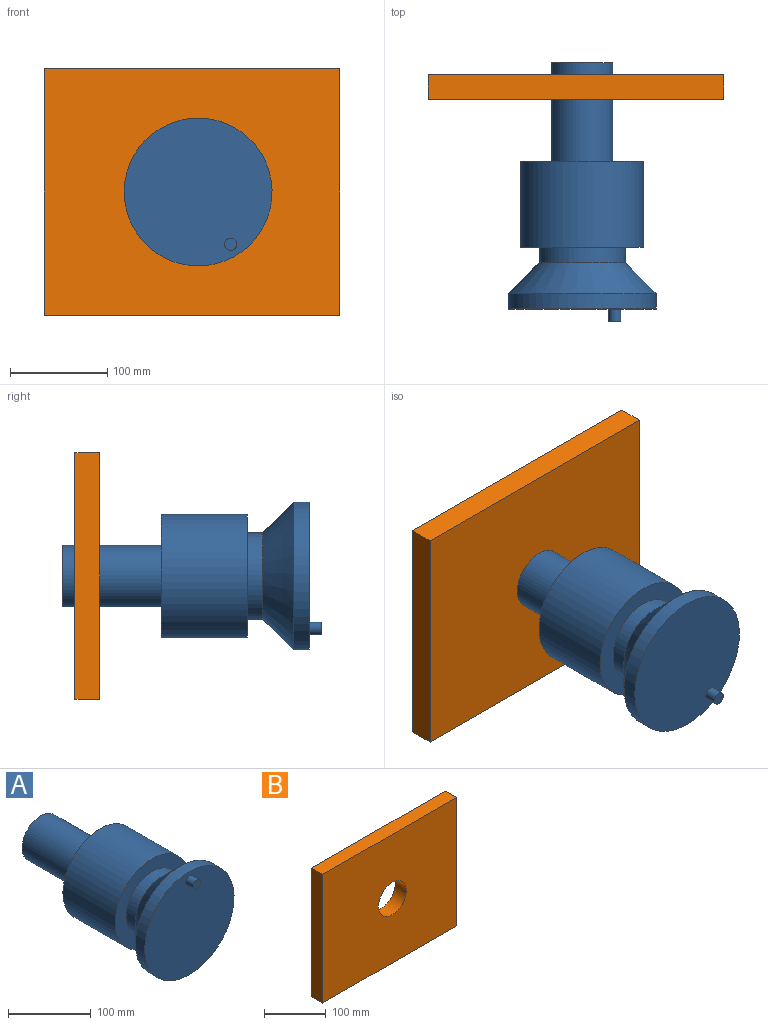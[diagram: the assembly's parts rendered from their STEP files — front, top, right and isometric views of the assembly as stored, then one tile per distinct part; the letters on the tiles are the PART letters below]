
ASSEMBLY  parts=2 mates=2
PART A: 11 faces, bbox 152.4x266.7x152.4 mm
  f0: cylinder r=76.2mm len=152.4mm, axis (0,-1,0), area 7600.6mm2, adj f1,f8
  f1: plane 152.4x152.4mm, normal (0,-1,0), area 18114.8mm2, adj f0,f9
  f2: plane 63.5x63.5mm, normal (0,1,0), area 3166.9mm2, adj f3
  f3: cylinder r=31.75mm len=101.6mm, axis (0,-1,0), area 20268.3mm2, adj f2,f4
  f4: plane 127x127mm, normal (0,1,0), area 9500.8mm2, adj f3,f5
  f5: cylinder r=63.5mm len=127mm, axis (0,-1,0), area 35469.5mm2, adj f4,f6
  f6: plane 127x127mm, normal (0,-1,0), area 6460.5mm2, adj f5,f7
  f7: cylinder r=44.45mm len=88.9mm, axis (0,-1,0), area 4433.7mm2, adj f6,f8
  f8: cone r=44.45mm half-angle=45deg, axis (0,-1,0), area 17019.1mm2, adj f0,f7
  f9: cylinder r=6.35mm len=12.7mm, axis (0,1,0), area 506.7mm2, adj f1,f10
  f10: plane 12.7x12.7mm, normal (0,-1,0), area 126.7mm2, adj f9
PART B: 7 faces, bbox 304.8x25.4x254 mm
  f0: plane 304.8x25.4mm, normal (0,0,1), area 7741.9mm2, adj f1,f4,f5,f6
  f1: plane 254x25.4mm, normal (-1,0,0), area 6451.6mm2, adj f0,f2,f5,f6
  f2: plane 304.8x25.4mm, normal (0,0,-1), area 7741.9mm2, adj f1,f4,f5,f6
  f3: cylinder r=31.75mm len=63.5mm, axis (0,1,0), area 5067.1mm2, adj f5,f6
  f4: plane 254x25.4mm, normal (1,0,0), area 6451.6mm2, adj f0,f2,f5,f6
  f5: plane 304.8x254mm, normal (0,-1,0), area 74252.3mm2, adj f0,f1,f2,f3,f4
  f6: plane 304.8x254mm, normal (0,1,0), area 74252.3mm2, adj f0,f1,f2,f3,f4
PLACE A rot(axis=(0,1,0),148deg) t=(-4.79,58.4,117.02)mm
PLACE B t=(-163.54,45.7,-9.98)mm fixed
MATE cylindrical A.f0 <-> B.f3  axis (0,-1,0) through (-4.79,7.6,117.02)mm
MATE planar B.f6 <-> A.f0  axis (0,1,0) through (-11.41,45.7,117.02)mm
